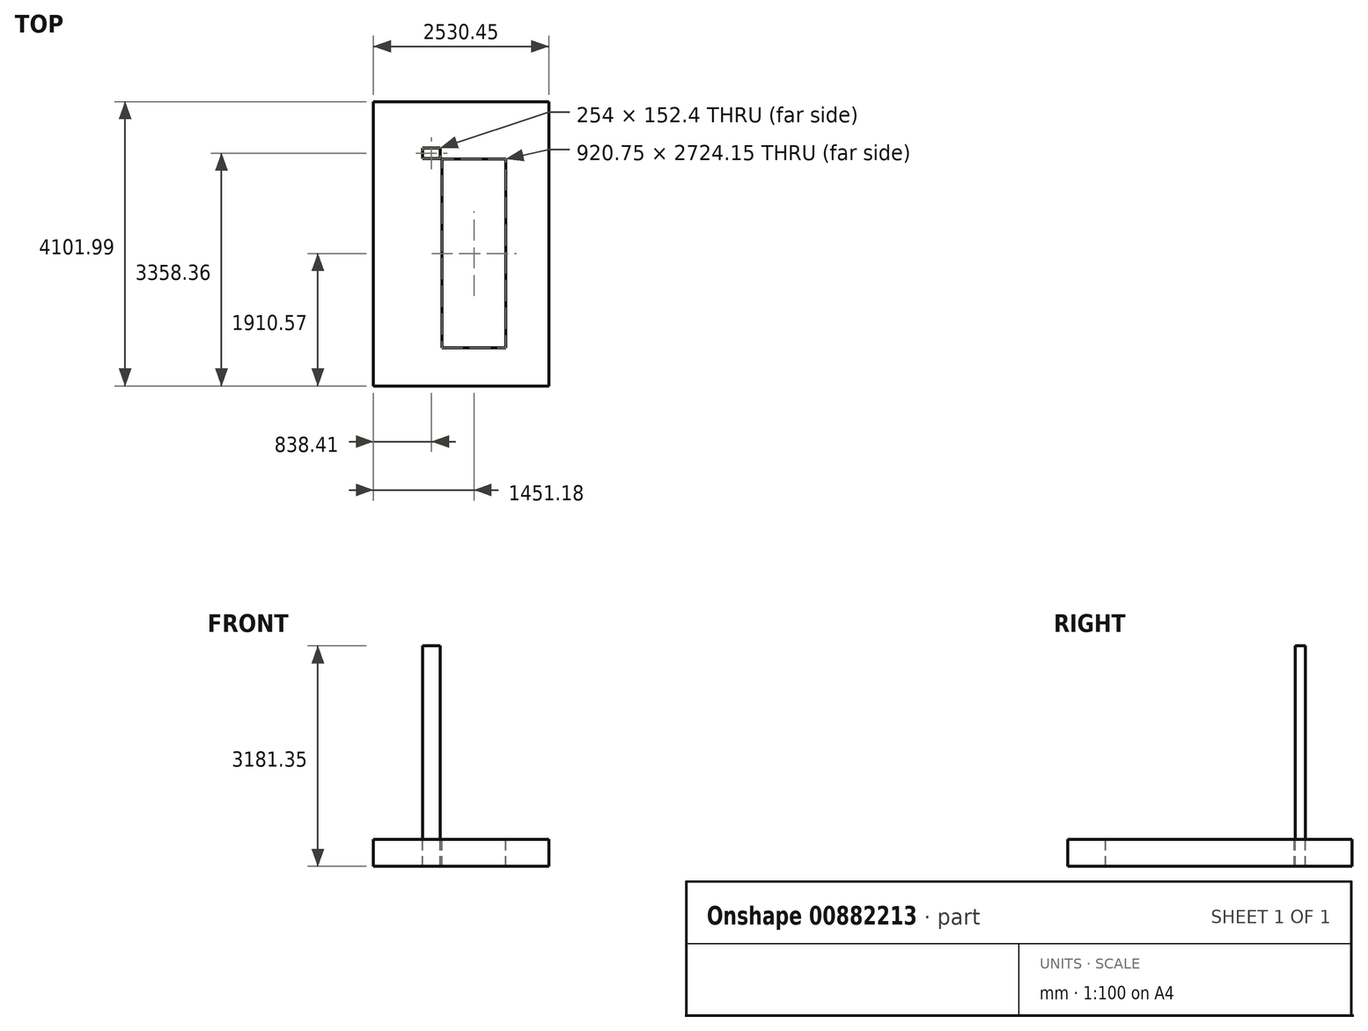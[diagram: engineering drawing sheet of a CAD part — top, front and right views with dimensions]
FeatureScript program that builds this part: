
annotation { "Feature Type Name" : "Feature", "Feature Type Description" : "" }
export const myFeature = defineFeature(function(context is Context, id is Id, definition is map)
    precondition{}
    {
        {
            var Q0;
            Q0=qCreatedBy(makeId("Top.planeOp"),FACE);
            var sketch = newSketch(context, id + "F0", { "sketchPlane" : qUnion([Q0])});
            skLineSegment(sketch, "E0.bottom", {"start": v(0, 0) * mm, "end": v(-920.75, 0) * mm});
            skLineSegment(sketch, "E0.top", {"start": v(0, -2724.15) * mm, "end": v(-920.75, -2724.15) * mm});
            skLineSegment(sketch, "E0.left", {"start": v(0, 0) * mm, "end": v(0, -2724.15) * mm});
            skLineSegment(sketch, "E0.right", {"start": v(-920.75, 0) * mm, "end": v(-920.75, -2724.15) * mm});
            skLineSegment(sketch, "E1.bottom", {"start": v(-1200.15, 161.93) * mm, "end": v(-946.15, 161.93) * mm});
            skLineSegment(sketch, "E1.top", {"start": v(-1200.15, 9.53) * mm, "end": v(-946.15, 9.53) * mm});
            skLineSegment(sketch, "E1.left", {"start": v(-1200.15, 161.93) * mm, "end": v(-1200.15, 9.53) * mm});
            skLineSegment(sketch, "E1.right", {"start": v(-946.15, 161.93) * mm, "end": v(-946.15, 9.53) * mm});
            skLineSegment(sketch, "E2.bottom", {"start": v(-1911.56, 829.35) * mm, "end": v(618.89, 829.35) * mm});
            skLineSegment(sketch, "E2.top", {"start": v(-1911.56, -3272.64) * mm, "end": v(618.89, -3272.64) * mm});
            skLineSegment(sketch, "E2.left", {"start": v(-1911.56, 829.35) * mm, "end": v(-1911.56, -3272.64) * mm});
            skLineSegment(sketch, "E2.right", {"start": v(618.89, 829.35) * mm, "end": v(618.89, -3272.64) * mm});
            skSolve(sketch);
        }
        {
            var Q0;
            Q0=makeQuery(id+"F0.imprint","IMPRINT",FACE,{"disambiguationData":[TD([[makeQuery(id+"F0.imprint","IMPRINT",EDGE,{"derivedFrom":sQuery(id+"F0.wireOp",EDGE,"E1.bottom")}),-1.0]])]});
            extrude(context, id + "F1", {"entities" : qUnion([Q0]), "depth" : 2794 * mm, "offsetDistance" : 25.4 * mm});
        }
        {
            var Q0;
            Q0=makeQuery(id+"F0.imprint","IMPRINT",FACE,{"disambiguationData":[TD([[makeQuery(id+"F0.imprint","IMPRINT",EDGE,{"derivedFrom":sQuery(id+"F0.wireOp",EDGE,"E0.bottom")}),-1.0]])]});
            var Q1;
            Q1 = qSketchRegion(id + "F0", true);
            var Q2;
            Q2=makeQuery(id+"F1.opExtrude","CAP_FACE",FACE,{"disambiguationData":[OSD([sQuery(id+"F0.wireOp",EDGE,"E1.bottom"),sQuery(id+"F0.wireOp",EDGE,"E1.top"),sQuery(id+"F0.wireOp",EDGE,"E1.left"),sQuery(id+"F0.wireOp",EDGE,"E1.right")])],"isStart":false});
            extrude(context, id + "F2", {"entities" : qUnion([Q0, Q1, Q2]), "operationType" : NewBodyOperationType.ADD, "oppositeDirection" : true, "depth" : 387.35 * mm, "offsetDistance" : 25.4 * mm});
        }
    });
